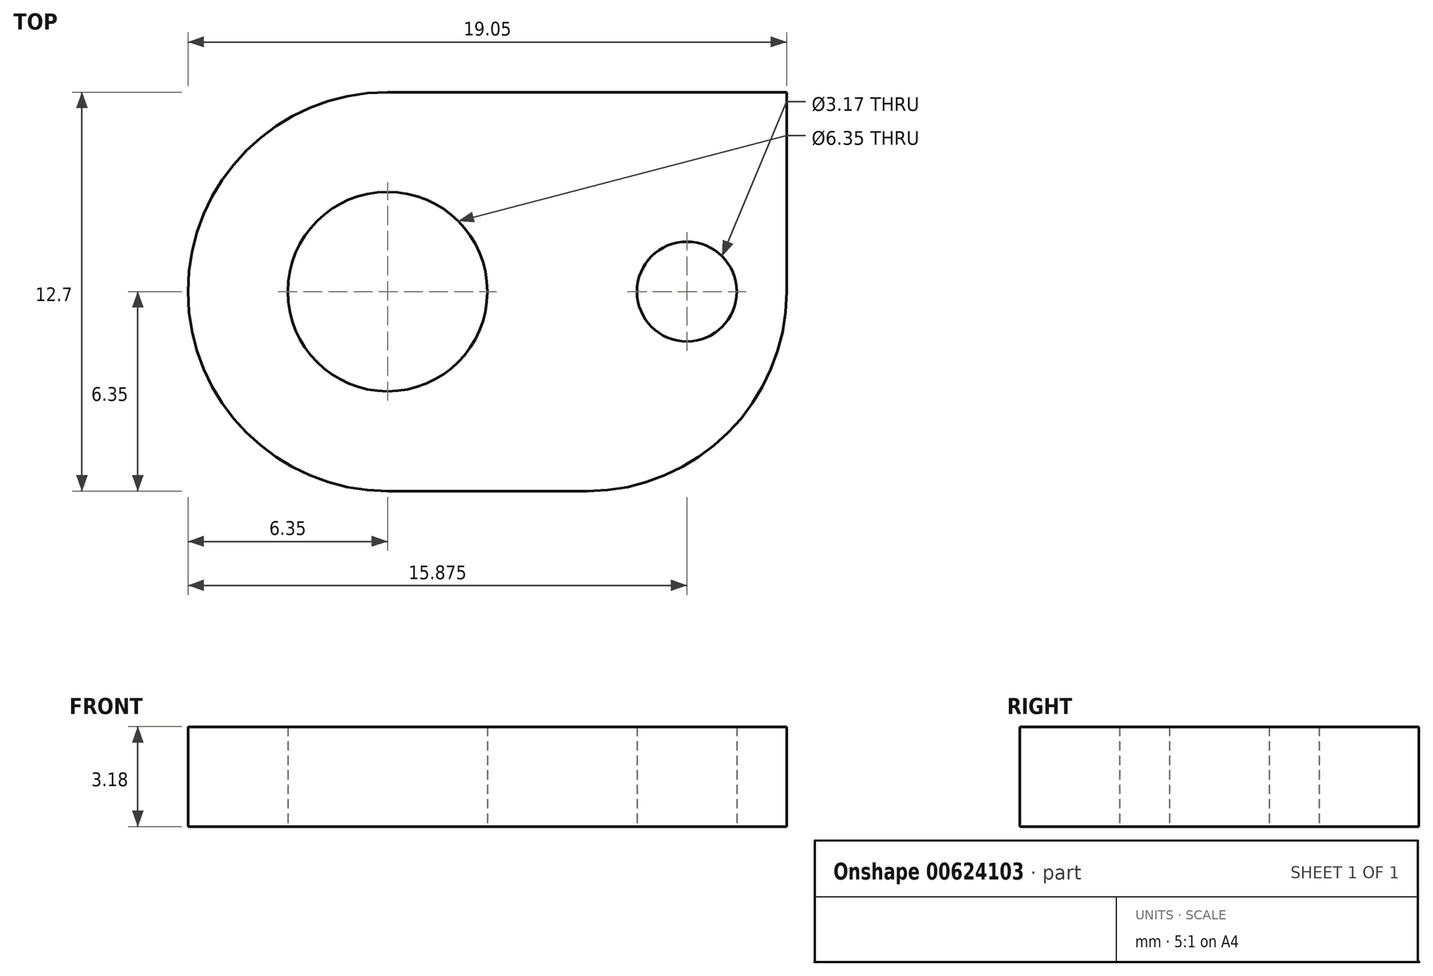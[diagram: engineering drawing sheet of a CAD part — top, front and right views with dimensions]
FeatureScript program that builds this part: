
annotation { "Feature Type Name" : "Feature", "Feature Type Description" : "" }
export const myFeature = defineFeature(function(context is Context, id is Id, definition is map)
    precondition{}
    {
        {
            var Q0;
            Q0=qCreatedBy(makeId("Top.planeOp"),FACE);
            var sketch = newSketch(context, id + "F0", { "sketchPlane" : qUnion([Q0])});
            skLineSegment(sketch, "E0.bottom", {"start": v(6.35, 0) * mm, "end": v(12.7, 0) * mm});
            skLineSegment(sketch, "E0.top", {"start": v(6.35, 12.7) * mm, "end": v(19.05, 12.7) * mm});
            skLineSegment(sketch, "E0.left", {"start": v(0, 6.35) * mm, "end": v(0, 6.35) * mm});
            skLineSegment(sketch, "E0.right", {"start": v(19.05, 6.35) * mm, "end": v(19.05, 12.7) * mm});
            skPoint(sketch, "E1.visualSharp", {"position": v(0, 0) * mm});
            skArc(sketch, "E1.filletArc", {"start": v(0, 6.35) * mm, "mid": v(1.86, 1.86) * mm, "end": v(6.35, 0) * mm});
            skPoint(sketch, "E2.visualSharp", {"position": v(0, 12.7) * mm});
            skArc(sketch, "E2.filletArc", {"start": v(6.35, 12.7) * mm, "mid": v(1.86, 10.84) * mm, "end": v(0, 6.35) * mm});
            skPoint(sketch, "E3.visualSharp", {"position": v(19.05, 0) * mm});
            skArc(sketch, "E3.filletArc", {"start": v(12.7, 0) * mm, "mid": v(17.2, 1.86) * mm, "end": v(19.05, 6.35) * mm});
            skLineSegment(sketch, "E4", {"start": v(6.35, 12.7) * mm, "end": v(6.35, 0) * mm});
            skCircle(sketch, "E5", {"center": v(6.35, 6.35) * mm, "radius": 3.18 * mm});
            skLineSegment(sketch, "E6", {"start": v(6.35, 6.35) * mm, "end": v(15.88, 6.35) * mm});
            skCircle(sketch, "E7", {"center": v(15.88, 6.35) * mm, "radius": 1.59 * mm});
            skSolve(sketch);
        }
        {
            var Q0;
            {var subQ5=sQuery(id+"F0.wireOp",EDGE,"E0.bottom");Q0=makeQuery(id+"F0.imprint","IMPRINT",FACE,{"disambiguationData":[TD([[makeQuery(id+"F0.imprint","IMPRINT",EDGE,{"derivedFrom":subQ5}),1.0]])]});}
            var Q1;
            {var subQ4=sQuery(id+"F0.wireOp",EDGE,"E1.filletArc");Q1=makeQuery(id+"F0.imprint","IMPRINT",FACE,{"disambiguationData":[TD([[makeQuery(id+"F0.imprint","IMPRINT",EDGE,{"derivedFrom":subQ4}),1.0]])]});}
            extrude(context, id + "F1", {"entities" : qUnion([Q0, Q1]), "depth" : 3.17 * mm, "offsetDistance" : 25.4 * mm});
        }
    });
